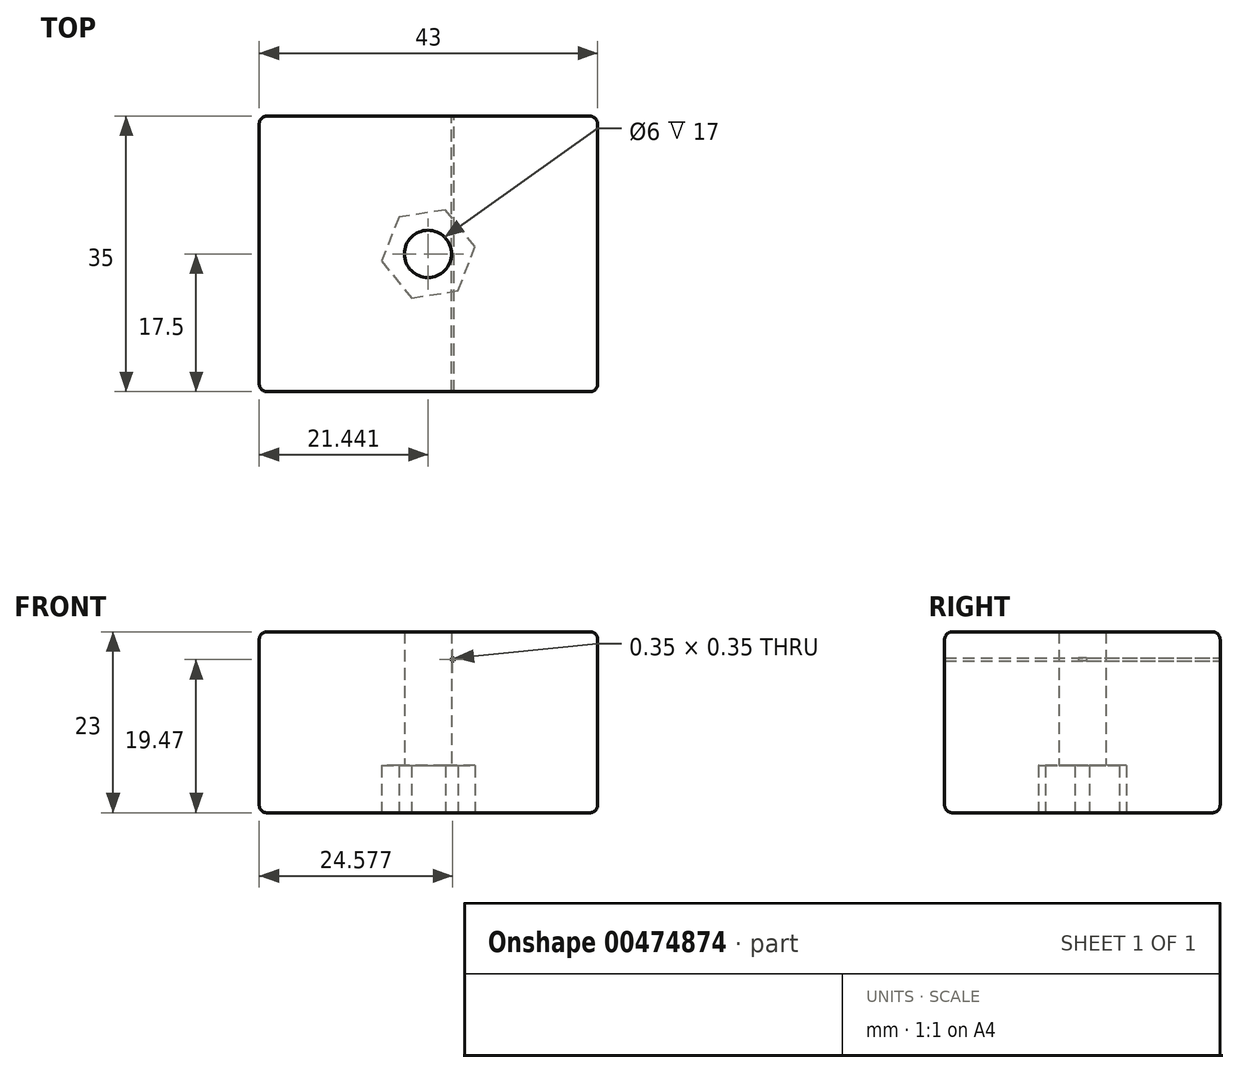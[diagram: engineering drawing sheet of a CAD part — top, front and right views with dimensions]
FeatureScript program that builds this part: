
annotation { "Feature Type Name" : "Feature", "Feature Type Description" : "" }
export const myFeature = defineFeature(function(context is Context, id is Id, definition is map)
    precondition{}
    {
        {
            var Q0;
            Q0=qCreatedBy(makeId("Front.planeOp"),FACE);
            var sketch = newSketch(context, id + "F0", { "sketchPlane" : qUnion([Q0])});
            skLineSegment(sketch, "E0.bottom", {"start": v(-31.82, 30.34) * mm, "end": v(8.18, 30.34) * mm});
            skLineSegment(sketch, "E0.top", {"start": v(-31.82, 7.34) * mm, "end": v(8.18, 7.34) * mm});
            skLineSegment(sketch, "E0.left", {"start": v(-31.82, 30.34) * mm, "end": v(-31.82, 7.34) * mm});
            skLineSegment(sketch, "E0.right", {"start": v(8.18, 30.34) * mm, "end": v(8.18, 7.34) * mm});
            skLineSegment(sketch, "E1.bottom", {"start": v(-10.07, 26.99) * mm, "end": v(-10.42, 26.99) * mm});
            skLineSegment(sketch, "E1.top", {"start": v(-10.07, 26.63) * mm, "end": v(-10.42, 26.63) * mm});
            skLineSegment(sketch, "E1.left", {"start": v(-10.07, 26.99) * mm, "end": v(-10.07, 26.63) * mm});
            skLineSegment(sketch, "E1.right", {"start": v(-10.42, 26.99) * mm, "end": v(-10.42, 26.63) * mm});
            skSolve(sketch);
        }
        {
            var Q0;
            Q0=makeQuery(id+"F0.imprint","IMPRINT",FACE,{"disambiguationData":[TD([[makeQuery(id+"F0.imprint","IMPRINT",EDGE,{"derivedFrom":sQuery(id+"F0.wireOp",EDGE,"E0.bottom")}),-1.0]])]});
            extrude(context, id + "F1", {"entities" : qUnion([Q0]), "depth" : 35 * mm});
        }
        {
            var Q0;
            Q0=makeQuery(id+"F1.opExtrude","SWEPT_FACE",FACE,{"disambiguationData":[OSD([sQuery(id+"F0.wireOp",EDGE,"E0.left")])]});
            extrude(context, id + "F2", {"entities" : qUnion([Q0]), "operationType" : NewBodyOperationType.ADD, "depth" : 3 * mm});
        }
        {
            var Q0;
            Q0=makeQuery(id+"F1.opExtrude","CAP_EDGE",EDGE,{"disambiguationData":[OSD([sQuery(id+"F0.wireOp",EDGE,"E0.bottom")])],"isStart":false});
            fillet(context, id + "F3", {"entities" : qUnion([Q0]), "radius" : 1 * mm, "tangentPropagation" : true, "allowEdgeOverflow" : false});
        }
        {
            var Q0;
            Q0=makeQuery(id+"F1.opExtrude","CAP_EDGE",EDGE,{"disambiguationData":[OSD([sQuery(id+"F0.wireOp",EDGE,"E0.top")])],"isStart":false});
            var Q1;
            Q1=makeQuery(id+"F1.opExtrude","SWEPT_EDGE",EDGE,{"disambiguationData":[OSD([sQuery(id+"F0.wireOp",EDGE,"E0.bottom"),sQuery(id+"F0.wireOp",EDGE,"E0.right")])]});
            var Q2;
            Q2=makeQuery(id+"F1.opExtrude","SWEPT_EDGE",EDGE,{"disambiguationData":[OSD([sQuery(id+"F0.wireOp",EDGE,"E0.top"),sQuery(id+"F0.wireOp",EDGE,"E0.right")])]});
            var Q3;
            Q3=makeQuery(id+"F1.opExtrude","CAP_EDGE",EDGE,{"disambiguationData":[OSD([sQuery(id+"F0.wireOp",EDGE,"E0.bottom")])],"isStart":true});
            var Q4;
            Q4=makeQuery(id+"F1.opExtrude","CAP_EDGE",EDGE,{"disambiguationData":[OSD([sQuery(id+"F0.wireOp",EDGE,"E0.top")])],"isStart":true});
            var Q5;
            Q5=makeQuery(id+"F1.opExtrude","SWEPT_EDGE",EDGE,{"disambiguationData":[OSD([sQuery(id+"F0.wireOp",EDGE,"E0.bottom"),sQuery(id+"F0.wireOp",EDGE,"E0.left")])]});
            var Q6;
            Q6=makeQuery(id+"F1.opExtrude","SWEPT_EDGE",EDGE,{"disambiguationData":[OSD([sQuery(id+"F0.wireOp",EDGE,"E0.top"),sQuery(id+"F0.wireOp",EDGE,"E0.left")])]});
            fillet(context, id + "F4", {"entities" : qUnion([Q0, Q1, Q2, Q3, Q4, Q5, Q6]), "radius" : 1 * mm, "tangentPropagation" : true, "allowEdgeOverflow" : false});
        }
        {
            var Q0;
            Q0=makeQuery(id+"F1.opExtrude","CAP_EDGE",EDGE,{"disambiguationData":[OSD([sQuery(id+"F0.wireOp",EDGE,"E0.right")])],"isStart":true});
            var Q1;
            Q1=makeQuery(id+"F1.opExtrude","CAP_EDGE",EDGE,{"disambiguationData":[OSD([sQuery(id+"F0.wireOp",EDGE,"E0.left")])],"isStart":true});
            fillet(context, id + "F5", {"entities" : qUnion([Q0, Q1]), "radius" : 1 * mm, "tangentPropagation" : true, "allowEdgeOverflow" : false});
        }
        {
            var Q0;
            Q0=makeQuery(id+"F2.opExtrude","CAP_EDGE",EDGE,{"disambiguationData":[OSD([sQuery(id+"F0.wireOp",EDGE,"E0.bottom"),sQuery(id+"F0.wireOp",EDGE,"E0.left")])],"isStart":false});
            fillet(context, id + "F6", {"entities" : qUnion([Q0]), "radius" : 1 * mm, "tangentPropagation" : true, "allowEdgeOverflow" : false});
        }
        {
            var Q0;
            {var subQ0=sQuery(id+"F0.wireOp",EDGE,"E0.top");Q0=makeQuery(id+"F2.boolean.opBoolean","MERGE",FACE,{"derivedFrom":[makeQuery(id+"F1.opExtrude","SWEPT_FACE",FACE,{"disambiguationData":[OSD([subQ0])]}),makeQuery(id+"F2.opExtrude","SWEPT_FACE",FACE,{"disambiguationData":[OSD([subQ0,sQuery(id+"F0.wireOp",EDGE,"E0.left")])]})]});}
            var sketch = newSketch(context, id + "F7", { "sketchPlane" : qUnion([Q0])});
            skLineSegment(sketch, "E2", {"start": v(-33.82, 34) * mm, "end": v(7.18, 1) * mm, "construction": true});
            skLineSegment(sketch, "E3", {"start": v(7.18, 34) * mm, "end": v(-33.82, 1) * mm, "construction": true});
            skCircle(sketch, "E4.cCircle", {"center": v(-13.32, 17.5) * mm, "radius": 5.2 * mm, "construction": true});
            skLineSegment(sketch, "E4.0", {"start": v(-19.25, 18.42) * mm, "end": v(-15.49, 23.1) * mm});
            skLineSegment(sketch, "E4.1", {"start": v(-15.49, 23.1) * mm, "end": v(-9.56, 22.17) * mm});
            skLineSegment(sketch, "E4.2", {"start": v(-9.56, 22.17) * mm, "end": v(-7.4, 16.58) * mm});
            skLineSegment(sketch, "E4.3", {"start": v(-7.4, 16.58) * mm, "end": v(-11.15, 11.9) * mm});
            skLineSegment(sketch, "E4.4", {"start": v(-11.15, 11.9) * mm, "end": v(-17.08, 12.83) * mm});
            skLineSegment(sketch, "E4.5", {"start": v(-17.08, 12.83) * mm, "end": v(-19.25, 18.42) * mm});
            skPoint(sketch, "E4.0.midPoint", {"position": v(-17.37, 20.76) * mm});
            skSolve(sketch);
        }
        {
            var Q0;
            Q0=makeQuery(id+"F7.imprint","IMPRINT",FACE,{"disambiguationData":[TD([[makeQuery(id+"F7.imprint","IMPRINT",EDGE,{"derivedFrom":sQuery(id+"F7.wireOp",EDGE,"E4.0")}),-1.0]])]});
            extrude(context, id + "F8", {"entities" : qUnion([Q0]), "operationType" : NewBodyOperationType.REMOVE, "oppositeDirection" : true, "depth" : 6 * mm, "offsetDistance" : 25 * mm});
        }
        {
            var Q0;
            Q0=makeQuery(id+"F8.boolean.opBoolean","COPY",FACE,{"derivedFrom":makeQuery(id+"F8.opExtrude","CAP_FACE",FACE,{"disambiguationData":[OSD([sQuery(id+"F7.wireOp",EDGE,"E4.0"),sQuery(id+"F7.wireOp",EDGE,"E4.1"),sQuery(id+"F7.wireOp",EDGE,"E4.2"),sQuery(id+"F7.wireOp",EDGE,"E4.3"),sQuery(id+"F7.wireOp",EDGE,"E4.4"),sQuery(id+"F7.wireOp",EDGE,"E4.5")])],"isStart":false})});
            var sketch = newSketch(context, id + "F9", { "sketchPlane" : qUnion([Q0])});
            skSolve(sketch);
        }
        {
            var Q0;
            Q0=makeQuery(id+"F9.imprint","IMPRINT",FACE,{"disambiguationData":[TD([[makeQuery(id+"F9.imprint","IMPRINT",EDGE,{"derivedFrom":makeQuery(id+"F8.boolean.opBoolean","COPY",EDGE,{"derivedFrom":makeQuery(id+"F8.opExtrude","CAP_EDGE",EDGE,{"disambiguationData":[OSD([sQuery(id+"F7.wireOp",EDGE,"E4.0")])],"isStart":false})})}),-1.0]])]});
            var sketch = newSketch(context, id + "F10", { "sketchPlane" : qUnion([Q0])});
            skCircle(sketch, "E5", {"center": v(-13.38, 17.5) * mm, "radius": 3 * mm});
            skSolve(sketch);
        }
        {
            var Q0;
            Q0=makeQuery(id+"F10.imprint","IMPRINT",FACE,{"disambiguationData":[TD([[makeQuery(id+"F10.imprint","IMPRINT",EDGE,{"derivedFrom":sQuery(id+"F10.wireOp",EDGE,"E5")}),1.0]])]});
            extrude(context, id + "F11", {"entities" : qUnion([Q0]), "operationType" : NewBodyOperationType.REMOVE, "endBound" : BoundingType.UP_TO_NEXT, "oppositeDirection" : true, "depth" : 25 * mm, "offsetDistance" : 25 * mm});
        }
    });
